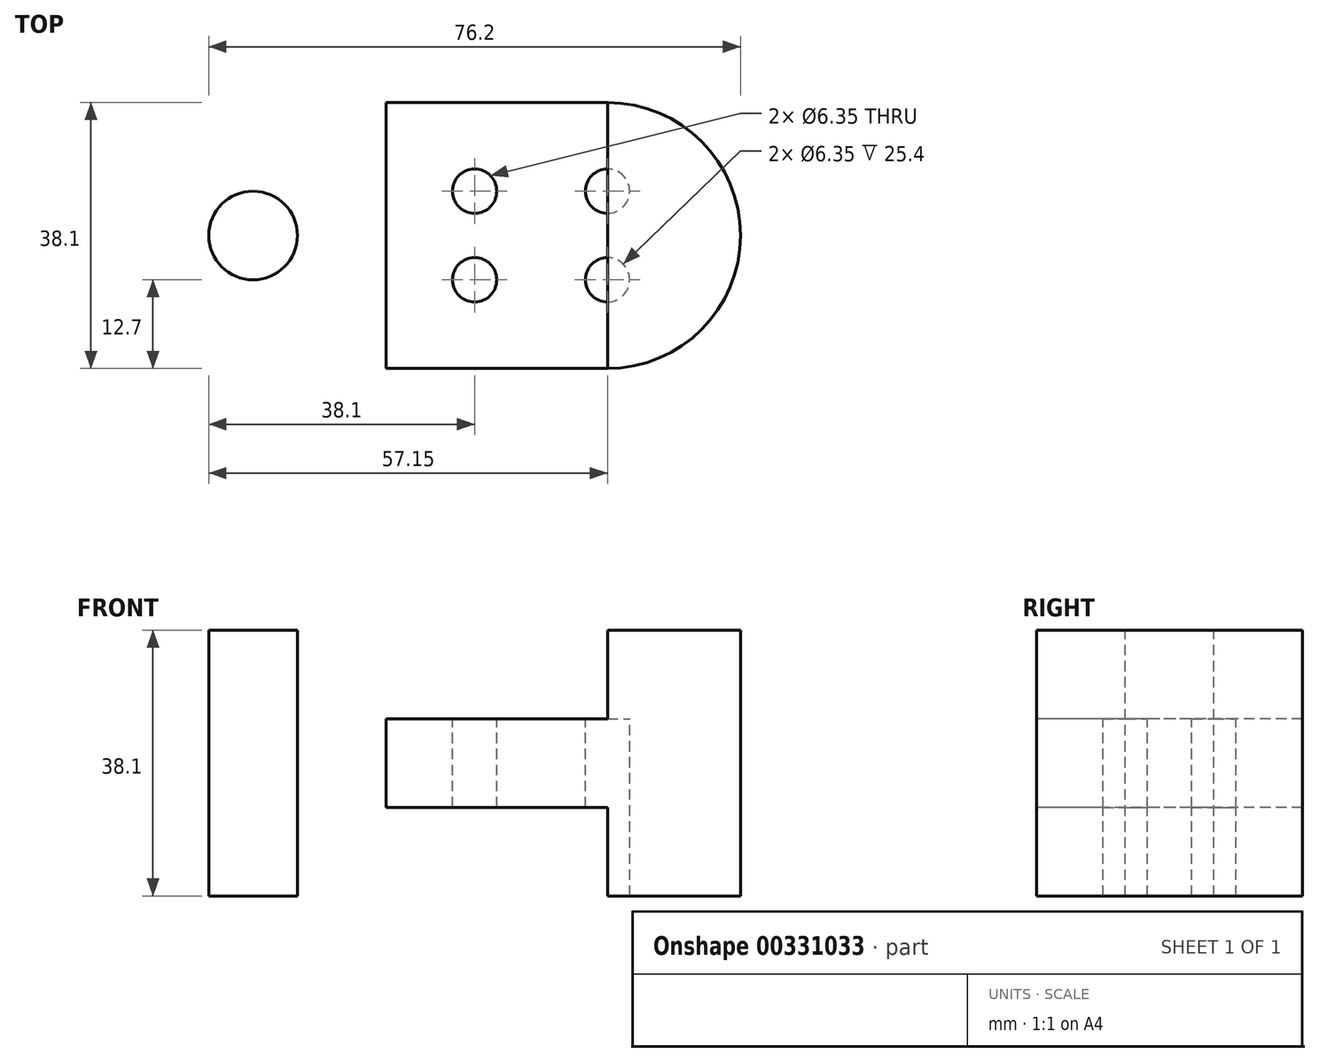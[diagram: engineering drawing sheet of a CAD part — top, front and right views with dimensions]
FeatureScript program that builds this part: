
annotation { "Feature Type Name" : "Feature", "Feature Type Description" : "" }
export const myFeature = defineFeature(function(context is Context, id is Id, definition is map)
    precondition{}
    {
        {
            var Q0;
            Q0=qCreatedBy(makeId("Top.planeOp"),FACE);
            var sketch = newSketch(context, id + "F0", { "sketchPlane" : qUnion([Q0])});
            skLineSegment(sketch, "E0", {"start": v(0, 0) * mm, "end": v(0, 19.05) * mm});
            skLineSegment(sketch, "E1", {"start": v(0, 19.05) * mm, "end": v(69.85, 19.05) * mm});
            skLineSegment(sketch, "E2", {"start": v(69.85, -19.05) * mm, "end": v(0, -19.05) * mm});
            skLineSegment(sketch, "E3", {"start": v(0, -19.05) * mm, "end": v(0, 0) * mm});
            skArc(sketch, "E4", {"start": v(69.85, -19.05) * mm, "mid": v(88.9, 0) * mm, "end": v(69.85, 19.05) * mm});
            skSolve(sketch);
        }
        {
            var Q0;
            Q0=makeQuery(id+"F0.imprint","IMPRINT",FACE,{"disambiguationData":[TD([[makeQuery(id+"F0.imprint","IMPRINT",EDGE,{"derivedFrom":sQuery(id+"F0.wireOp",EDGE,"E0")}),-1.0]])]});
            extrude(context, id + "F1", {"entities" : qUnion([Q0]), "endBound" : BoundingType.SYMMETRIC, "depth" : 38.1 * mm});
        }
        {
            var Q0;
            Q0=makeQuery(id+"F1.opExtrude","SWEPT_FACE",FACE,{"disambiguationData":[OSD([sQuery(id+"F0.wireOp",EDGE,"E2")])]});
            var sketch = newSketch(context, id + "F2", { "sketchPlane" : qUnion([Q0])});
            skLineSegment(sketch, "E5.0.0", {"start": v(0, -19.05) * mm, "end": v(69.85, -19.05) * mm});
            skLineSegment(sketch, "E5.0.1", {"start": v(69.85, -19.05) * mm, "end": v(69.85, 19.05) * mm});
            skLineSegment(sketch, "E5.0.2", {"start": v(69.85, 19.05) * mm, "end": v(0, 19.05) * mm});
            skLineSegment(sketch, "E5.0.3", {"start": v(0, 19.05) * mm, "end": v(0, -19.05) * mm});
            skLineSegment(sketch, "E6", {"start": v(88.9, 19.05) * mm, "end": v(88.9, -19.05) * mm});
            skLineSegment(sketch, "E7", {"start": v(88.9, 19.05) * mm, "end": v(38.1, 19.05) * mm});
            skLineSegment(sketch, "E8", {"start": v(38.1, 19.05) * mm, "end": v(38.1, 6.35) * mm});
            skLineSegment(sketch, "E9", {"start": v(38.1, 6.35) * mm, "end": v(88.9, 6.35) * mm});
            skLineSegment(sketch, "E10", {"start": v(88.9, 6.35) * mm, "end": v(88.9, 19.05) * mm});
            skLineSegment(sketch, "E11", {"start": v(88.9, -19.05) * mm, "end": v(38.1, -19.05) * mm});
            skLineSegment(sketch, "E12", {"start": v(38.1, -19.05) * mm, "end": v(38.1, -6.35) * mm});
            skLineSegment(sketch, "E13", {"start": v(38.1, -6.35) * mm, "end": v(88.9, -6.35) * mm});
            skLineSegment(sketch, "E14", {"start": v(88.9, -6.35) * mm, "end": v(88.9, -19.05) * mm});
            skSolve(sketch);
        }
        {
            var Q0;
            {var subQ5=sQuery(id+"F2.wireOp",EDGE,"E8");Q0=makeQuery(id+"F2.imprint","IMPRINT",FACE,{"disambiguationData":[TD([[makeQuery(id+"F2.imprint","IMPRINT",EDGE,{"derivedFrom":subQ5}),1.0]])]});}
            var Q1;
            {var subQ5=sQuery(id+"F2.wireOp",EDGE,"E10");Q1=makeQuery(id+"F2.imprint","IMPRINT",FACE,{"disambiguationData":[TD([[makeQuery(id+"F2.imprint","IMPRINT",EDGE,{"derivedFrom":subQ5}),1.0]])]});}
            var Q2;
            {var subQ5=sQuery(id+"F2.wireOp",EDGE,"E12");Q2=makeQuery(id+"F2.imprint","IMPRINT",FACE,{"disambiguationData":[TD([[makeQuery(id+"F2.imprint","IMPRINT",EDGE,{"derivedFrom":subQ5}),-1.0]])]});}
            var Q3;
            {var subQ5=sQuery(id+"F2.wireOp",EDGE,"E14");Q3=makeQuery(id+"F2.imprint","IMPRINT",FACE,{"disambiguationData":[TD([[makeQuery(id+"F2.imprint","IMPRINT",EDGE,{"derivedFrom":subQ5}),-1.0]])]});}
            extrude(context, id + "F3", {"entities" : qUnion([Q0, Q1, Q2, Q3]), "operationType" : NewBodyOperationType.REMOVE, "oppositeDirection" : true, "depth" : 50.8 * mm});
        }
        {
            var Q0;
            Q0=makeQuery(id+"F3.boolean.opBoolean","COPY",FACE,{"derivedFrom":makeQuery(id+"F3.opExtrude","SWEPT_FACE",FACE,{"disambiguationData":[OSD([sQuery(id+"F2.wireOp",EDGE,"E9")])]})});
            var sketch = newSketch(context, id + "F4", { "sketchPlane" : qUnion([Q0])});
            skArc(sketch, "E15.0.0", {"start": v(69.85, -19.05) * mm, "mid": v(88.9, 0) * mm, "end": v(69.85, 19.05) * mm});
            skLineSegment(sketch, "E15.0.1", {"start": v(69.85, 19.05) * mm, "end": v(38.1, 19.05) * mm});
            skLineSegment(sketch, "E15.0.2", {"start": v(38.1, 19.05) * mm, "end": v(38.1, -19.05) * mm});
            skLineSegment(sketch, "E15.0.3", {"start": v(38.1, -19.05) * mm, "end": v(69.85, -19.05) * mm});
            skCircle(sketch, "E16", {"center": v(50.8, 6.35) * mm, "radius": 3.18 * mm});
            skCircle(sketch, "E17.0.1.0", {"center": v(50.8, -6.35) * mm, "radius": 3.18 * mm});
            skCircle(sketch, "E17.1.0.0", {"center": v(69.85, 6.35) * mm, "radius": 3.18 * mm});
            skCircle(sketch, "E17.1.1.0", {"center": v(69.85, -6.35) * mm, "radius": 3.18 * mm});
            skLineSegment(sketch, "E17.direction1", {"start": v(50.8, 6.35) * mm, "end": v(69.85, 6.35) * mm, "construction": true});
            skLineSegment(sketch, "E17.direction2", {"start": v(50.8, 6.35) * mm, "end": v(50.8, -6.35) * mm, "construction": true});
            skSolve(sketch);
        }
        {
            var Q0;
            Q0=makeQuery(id+"F4.imprint","IMPRINT",FACE,{"disambiguationData":[TD([[makeQuery(id+"F4.imprint","IMPRINT",EDGE,{"derivedFrom":sQuery(id+"F4.wireOp",EDGE,"E16")}),1.0]])]});
            var Q1;
            Q1=makeQuery(id+"F4.imprint","IMPRINT",FACE,{"disambiguationData":[TD([[makeQuery(id+"F4.imprint","IMPRINT",EDGE,{"derivedFrom":sQuery(id+"F4.wireOp",EDGE,"E17.1.0.0")}),1.0]])]});
            var Q2;
            Q2=makeQuery(id+"F4.imprint","IMPRINT",FACE,{"disambiguationData":[TD([[makeQuery(id+"F4.imprint","IMPRINT",EDGE,{"derivedFrom":sQuery(id+"F4.wireOp",EDGE,"E17.1.1.0")}),1.0]])]});
            var Q3;
            Q3=makeQuery(id+"F4.imprint","IMPRINT",FACE,{"disambiguationData":[TD([[makeQuery(id+"F4.imprint","IMPRINT",EDGE,{"derivedFrom":sQuery(id+"F4.wireOp",EDGE,"E17.0.1.0")}),1.0]])]});
            extrude(context, id + "F5", {"entities" : qUnion([Q0, Q1, Q2, Q3]), "operationType" : NewBodyOperationType.REMOVE, "oppositeDirection" : true, "depth" : 25.4 * mm});
        }
        {
            var Q0;
            Q0=makeQuery(id+"F1.opExtrude","CAP_FACE",FACE,{"disambiguationData":[OSD([sQuery(id+"F0.wireOp",EDGE,"E0"),sQuery(id+"F0.wireOp",EDGE,"E1"),sQuery(id+"F0.wireOp",EDGE,"E2"),sQuery(id+"F0.wireOp",EDGE,"E3"),sQuery(id+"F0.wireOp",EDGE,"E4")])],"isStart":false});
            var sketch = newSketch(context, id + "F6", { "sketchPlane" : qUnion([Q0])});
            skLineSegment(sketch, "E18.0.0", {"start": v(38.1, -19.05) * mm, "end": v(38.1, 19.05) * mm});
            skLineSegment(sketch, "E18.0.1", {"start": v(38.1, 19.05) * mm, "end": v(0, 19.05) * mm});
            skLineSegment(sketch, "E18.0.2", {"start": v(0, 19.05) * mm, "end": v(0, -19.05) * mm});
            skLineSegment(sketch, "E18.0.3", {"start": v(0, -19.05) * mm, "end": v(38.1, -19.05) * mm});
            skLineSegment(sketch, "E19", {"start": v(0, 0) * mm, "end": v(38.1, 0) * mm});
            skCircle(sketch, "E20", {"center": v(19.05, 0) * mm, "radius": 6.35 * mm});
            skSolve(sketch);
        }
        {
            var Q0;
            {var subQ0=sQuery(id+"F6.wireOp",EDGE,"E20");var subQ1=sQuery(id+"F6.wireOp",EDGE,"E19");var subQ2=makeQuery(id+"F6.imprint","INTERSECT",VERTEX,{"disambiguationData":[OD(0.0)],"derivedFrom":[subQ1,subQ0]});Q0=makeQuery(id+"F6.imprint","IMPRINT",FACE,{"disambiguationData":[TD([[makeQuery(id+"F6.imprint","IMPRINT",EDGE,{"disambiguationData":[TD([[subQ2,-1.0]])],"derivedFrom":subQ1}),1.0]])]});}
            var Q1;
            {var subQ0=sQuery(id+"F6.wireOp",EDGE,"E20");var subQ1=sQuery(id+"F6.wireOp",EDGE,"E19");var subQ2=makeQuery(id+"F6.imprint","INTERSECT",VERTEX,{"disambiguationData":[OD(0.0)],"derivedFrom":[subQ1,subQ0]});Q1=makeQuery(id+"F6.imprint","IMPRINT",FACE,{"disambiguationData":[TD([[makeQuery(id+"F6.imprint","IMPRINT",EDGE,{"disambiguationData":[TD([[subQ2,-1.0]])],"derivedFrom":subQ1}),-1.0]])]});}
            extrude(context, id + "F7", {"entities" : qUnion([Q0, Q1]), "operationType" : NewBodyOperationType.REMOVE, "oppositeDirection" : true, "depth" : 38.1 * mm});
        }
    });
